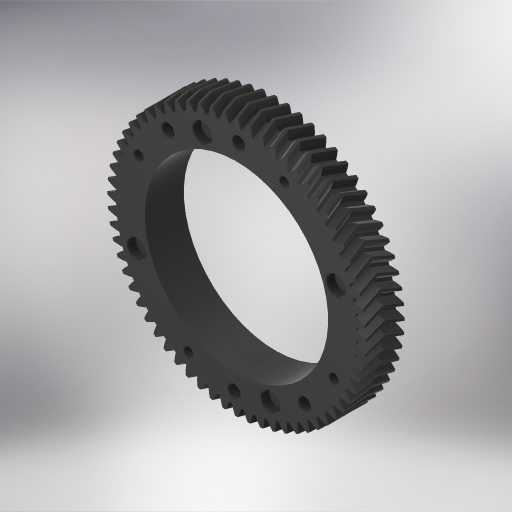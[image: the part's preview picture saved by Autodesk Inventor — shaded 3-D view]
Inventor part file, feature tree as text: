
AUTODESK INVENTOR PART (.ipt)
format: ipt  version: 2023.4 (Build 274418000, 418)  size: 1,587,712 bytes
history: native  units: in
note: dims shown in document units (in); Inventor stores cm internally (conversion verified against a paired STEP export)
features: sketch x4, hole x3, other x2, extrude x1
ambient origin geometry x8: Origin, YZ Plane, XZ Plane, XY Plane, X Axis, Y Axis, Z Axis, Center Point
bodies: Solid1 (feature_tree)
feature tree (10):
  other  "Helical 2M 64T"
  sketch  "Sketch1"  dims[d0=4.7244in d1=3.7in]
  extrude  "Extrusion1"  Depth=3.7in
  other  "DIAMETRIC PITCH"
  hole  "Hole5"  [1 undecoded]
  hole  "Hole6"  [1 undecoded]
  hole  "Hole7"  [1 undecoded]
  sketch  "Sketch7"  dims[d12=1.0in d13=0.0in d14=5.0394in]
  sketch  "Sketch8"  dims[d25=2.1875in d51=4.375in]
  sketch  "Sketch9"  dims[d54=0.75in d55=0.75in d56=0.261in d57=0.5in d58=0.119in d59=0.25in d60=0.5635in d61=1.0in d62=0.0in d64=1.5748in d66=360.0deg d68=0.201in d69=0.75in d70=0.375in d71=0.25in d72=0.5635in d73=1.0in d74=0.0in d75=1.5748in d77=360.0deg d79=4.24in d80=45.0deg d81=1.5748in d83=360.0deg d85=0.4in d86=0.75in d87=0.375in d88=0.25in d89=0.5635in d90=0.17in d91=0.0in]
note: 3 required parameter values undecoded (feature->parameter linkage not recoverable at this tier; creation-order binding heuristic only, values carry confidence <= 0.55)
